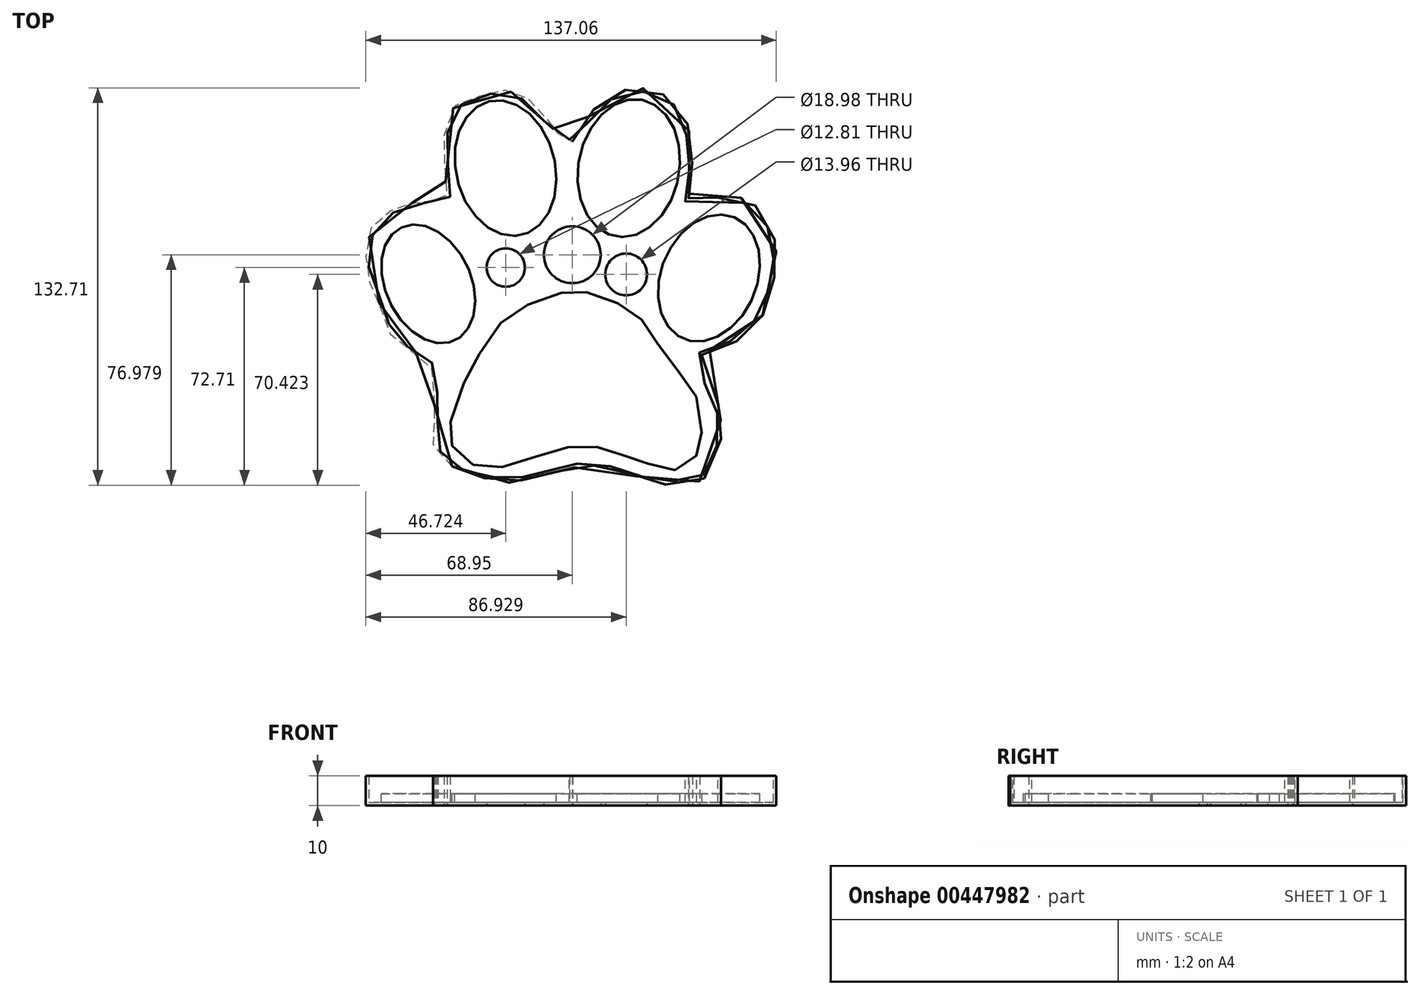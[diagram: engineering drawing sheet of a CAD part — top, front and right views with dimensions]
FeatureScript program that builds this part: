
annotation { "Feature Type Name" : "Feature", "Feature Type Description" : "" }
export const myFeature = defineFeature(function(context is Context, id is Id, definition is map)
    precondition{}
    {
        {
            var Q0;
            Q0=qCreatedBy(makeId("Top.planeOp"),FACE);
            var sketch = newSketch(context, id + "F0", { "sketchPlane" : qUnion([Q0])});
            skFitSpline(sketch, "E0", {"points": [v(-40.16, -66.43) * mm, v(-46.1, -59.99) * mm, v(-46.1, -54.04) * mm, v(-46.1, -44.62) * mm, v(-46.1, -41.64) * mm, v(-46.1, -36.2) * mm, v(-50.57, -29.25) * mm, v(-56.52, -26.77) * mm, v(-61.47, -20.82) * mm, v(-63.95, -13.39) * mm, v(-66.93, -6.44) * mm, v(-68.9, 0) * mm, v(-67.92, 9.42) * mm, v(-65.94, 15.37) * mm, v(-59.99, 19.33) * mm, v(-55.52, 20.82) * mm, v(-51.06, 22.3) * mm, v(-45.11, 22.3) * mm, v(-42.14, 22.3) * mm, v(-42.14, 27.27) * mm, v(-42.63, 38.17) * mm, v(-42.63, 45.11) * mm, v(-38.67, 54.53) * mm, v(-32.72, 56.52) * mm, v(-25.78, 59.5) * mm, v(-19.83, 58.5) * mm, v(-14.87, 56.52) * mm, v(-10.41, 52.05) * mm, v(-6.94, 47.1) * mm, v(-4.96, 45.11) * mm, v(0, 43.13) * mm, v(0, 42.14) * mm, v(3.47, 47.6) * mm, v(8.43, 54.04) * mm, v(14.38, 58) * mm, v(21.32, 59.99) * mm, v(28.75, 58.5) * mm, v(35.7, 54.04) * mm, v(38.67, 47.1) * mm, v(39.66, 39.16) * mm, v(40.16, 32.72) * mm, v(39.66, 27.76) * mm, v(39.16, 20.82) * mm, v(45.11, 22.3) * mm, v(53.54, 23.8) * mm, v(60.98, 20.82) * mm, v(65.94, 14.38) * mm, v(67.92, 6.94) * mm, v(67.92, 0) * mm, v(66.43, -7.93) * mm, v(63.95, -15.37) * mm, v(60.98, -18.84) * mm, v(54.53, -24.79) * mm, v(47.6, -27.27) * mm, v(42.63, -30.24) * mm, v(48.58, -45.6) * mm, v(49.58, -51.56) * mm, v(49.58, -57.5) * mm, v(46.6, -67.42) * mm, v(41.15, -71.88) * mm, v(32.72, -72.38) * mm, v(25.78, -72.38) * mm, v(19.83, -68.9) * mm, v(12.89, -67.42) * mm, v(5.45, -65.94) * mm, v(0, -66.93) * mm, v(-5.95, -68.41) * mm, v(-14.38, -70.4) * mm, v(-22.8, -71.88) * mm, v(-28.75, -70.4) * mm, v(-34.7, -69.4) * mm, v(-40.16, -66.43) * mm]});
            skEllipse(sketch, "E1", {"center": v(-22.3, 33.22) * mm, "majorRadius": 22.97 * mm, "minorRadius": 16.57 * mm, "majorAxis": v(-0.24, 0.97)});
            skEllipse(sketch, "E2", {"center": v(18.84, 33.22) * mm, "majorRadius": 23.24 * mm, "minorRadius": 16.88 * mm, "majorAxis": v(0.2, 0.98)});
            skEllipse(sketch, "E3", {"center": v(45.6, -3.47) * mm, "majorRadius": 22 * mm, "minorRadius": 16.02 * mm, "majorAxis": v(0.38, 0.92)});
            skEllipse(sketch, "E4", {"center": v(-48.09, -5.45) * mm, "majorRadius": 20.85 * mm, "minorRadius": 14.3 * mm, "majorAxis": v(-0.43, 0.9)});
            skFitSpline(sketch, "E5", {"points": [v(-40.65, -51.56) * mm, v(-36.69, -39.66) * mm, v(-33.22, -32.72) * mm, v(-28.26, -24.3) * mm, v(-22.3, -16.86) * mm, v(-15.86, -12.89) * mm, v(-7.44, -9.42) * mm, v(0, -7.93) * mm, v(3.47, -7.93) * mm, v(9.92, -9.92) * mm, v(17.35, -12.89) * mm, v(22.3, -16.36) * mm, v(25.78, -21.32) * mm, v(29.75, -27.27) * mm, v(34.65, -33.54) * mm, v(38.92, -40.04) * mm, v(42.63, -45.6) * mm, v(43.19, -56.2) * mm, v(42.82, -60.65) * mm, v(40.77, -63.43) * mm, v(37.25, -66.59) * mm, v(31.68, -67.7) * mm, v(26.48, -65.85) * mm, v(20.9, -64.18) * mm, v(16.08, -62.32) * mm, v(11.06, -60.65) * mm, v(6.23, -59.53) * mm, v(0, -59.72) * mm, v(-7.5, -61.58) * mm, v(-16.23, -64.55) * mm, v(-24.4, -66.78) * mm, v(-30.35, -66.78) * mm, v(-36.3, -64) * mm, v(-40, -59.9) * mm, v(-40.19, -55.45) * mm, v(-40.65, -51.56) * mm]});
            skSolve(sketch);
        }
        {
            var Q0;
            Q0=makeQuery(id+"F0.imprint","IMPRINT",FACE,{"disambiguationData":[TD([[makeQuery(id+"F0.imprint","IMPRINT",EDGE,{"derivedFrom":sQuery(id+"F0.wireOp",EDGE,"E0")}),-1.0]])]});
            var Q1;
            Q1=makeQuery(id+"F0.imprint","IMPRINT",FACE,{"disambiguationData":[TD([[makeQuery(id+"F0.imprint","IMPRINT",EDGE,{"derivedFrom":sQuery(id+"F0.wireOp",EDGE,"E1")}),1.0]])]});
            var Q2;
            Q2=makeQuery(id+"F0.imprint","IMPRINT",FACE,{"disambiguationData":[TD([[makeQuery(id+"F0.imprint","IMPRINT",EDGE,{"derivedFrom":sQuery(id+"F0.wireOp",EDGE,"E4")}),1.0]])]});
            var Q3;
            Q3=makeQuery(id+"F0.imprint","IMPRINT",FACE,{"disambiguationData":[TD([[makeQuery(id+"F0.imprint","IMPRINT",EDGE,{"derivedFrom":sQuery(id+"F0.wireOp",EDGE,"E2")}),1.0]])]});
            var Q4;
            Q4=makeQuery(id+"F0.imprint","IMPRINT",FACE,{"disambiguationData":[TD([[makeQuery(id+"F0.imprint","IMPRINT",EDGE,{"derivedFrom":sQuery(id+"F0.wireOp",EDGE,"E3")}),1.0]])]});
            var Q5;
            Q5=makeQuery(id+"F0.imprint","IMPRINT",FACE,{"disambiguationData":[TD([[makeQuery(id+"F0.imprint","IMPRINT",EDGE,{"derivedFrom":sQuery(id+"F0.wireOp",EDGE,"E5")}),-1.0]])]});
            extrude(context, id + "F1", {"entities" : qUnion([Q0, Q1, Q2, Q3, Q4, Q5]), "depth" : 10 * mm});
        }
        {
            var Q0;
            Q0=makeQuery(id+"F1.opExtrude","CAP_FACE",FACE,{"disambiguationData":[OSD([sQuery(id+"F0.wireOp",EDGE,"E0")])],"isStart":false});
            shell(context, id + "F2", {"entities" : qUnion([Q0]), "thickness" : 1 * mm});
        }
        {
            var Q0;
            Q0=makeQuery(id+"F0.imprint","IMPRINT",FACE,{"disambiguationData":[TD([[makeQuery(id+"F0.imprint","IMPRINT",EDGE,{"derivedFrom":sQuery(id+"F0.wireOp",EDGE,"E3")}),1.0]])]});
            var Q1;
            Q1=makeQuery(id+"F0.imprint","IMPRINT",FACE,{"disambiguationData":[TD([[makeQuery(id+"F0.imprint","IMPRINT",EDGE,{"derivedFrom":sQuery(id+"F0.wireOp",EDGE,"E2")}),1.0]])]});
            var Q2;
            Q2=makeQuery(id+"F0.imprint","IMPRINT",FACE,{"disambiguationData":[TD([[makeQuery(id+"F0.imprint","IMPRINT",EDGE,{"derivedFrom":sQuery(id+"F0.wireOp",EDGE,"E1")}),1.0]])]});
            var Q3;
            Q3=makeQuery(id+"F0.imprint","IMPRINT",FACE,{"disambiguationData":[TD([[makeQuery(id+"F0.imprint","IMPRINT",EDGE,{"derivedFrom":sQuery(id+"F0.wireOp",EDGE,"E4")}),1.0]])]});
            var Q4;
            Q4=makeQuery(id+"F0.imprint","IMPRINT",FACE,{"disambiguationData":[TD([[makeQuery(id+"F0.imprint","IMPRINT",EDGE,{"derivedFrom":sQuery(id+"F0.wireOp",EDGE,"E5")}),-1.0]])]});
            extrude(context, id + "F3", {"entities" : qUnion([Q0, Q1, Q2, Q3, Q4]), "operationType" : NewBodyOperationType.ADD, "depth" : 4 * mm});
        }
        {
            var Q0;
            Q0=qCreatedBy(makeId("Top.planeOp"),FACE);
            var sketch = newSketch(context, id + "F4", { "sketchPlane" : qUnion([Q0])});
            skCircle(sketch, "E6", {"center": v(0, 4.27) * mm, "radius": 9.5 * mm});
            skCircle(sketch, "E7", {"center": v(-22.23, 0) * mm, "radius": 6.4 * mm});
            skCircle(sketch, "E8", {"center": v(17.98, -2.29) * mm, "radius": 6.98 * mm});
            skSolve(sketch);
        }
        {
            var Q0;
            Q0=makeQuery(id+"F4.imprint","IMPRINT",FACE,{"disambiguationData":[TD([[makeQuery(id+"F4.imprint","IMPRINT",EDGE,{"derivedFrom":sQuery(id+"F4.wireOp",EDGE,"E6")}),1.0]])]});
            var Q1;
            Q1=makeQuery(id+"F4.imprint","IMPRINT",FACE,{"disambiguationData":[TD([[makeQuery(id+"F4.imprint","IMPRINT",EDGE,{"derivedFrom":sQuery(id+"F4.wireOp",EDGE,"E7")}),1.0]])]});
            var Q2;
            Q2=makeQuery(id+"F4.imprint","IMPRINT",FACE,{"disambiguationData":[TD([[makeQuery(id+"F4.imprint","IMPRINT",EDGE,{"derivedFrom":sQuery(id+"F4.wireOp",EDGE,"E8")}),1.0]])]});
            var Q3;
            Q3=sQuery(id+"F4.wireOp",EDGE,"E8");
            var Q4;
            Q4=sQuery(id+"F4.wireOp",EDGE,"E6");
            var Q5;
            Q5=sQuery(id+"F4.wireOp",EDGE,"E7");
            extrude(context, id + "F5", {"entities" : qUnion([Q0, Q1, Q2]), "operationType" : NewBodyOperationType.REMOVE, "surfaceEntities" : qUnion([Q3, Q4, Q5]), "depth" : 25 * mm});
        }
    });
